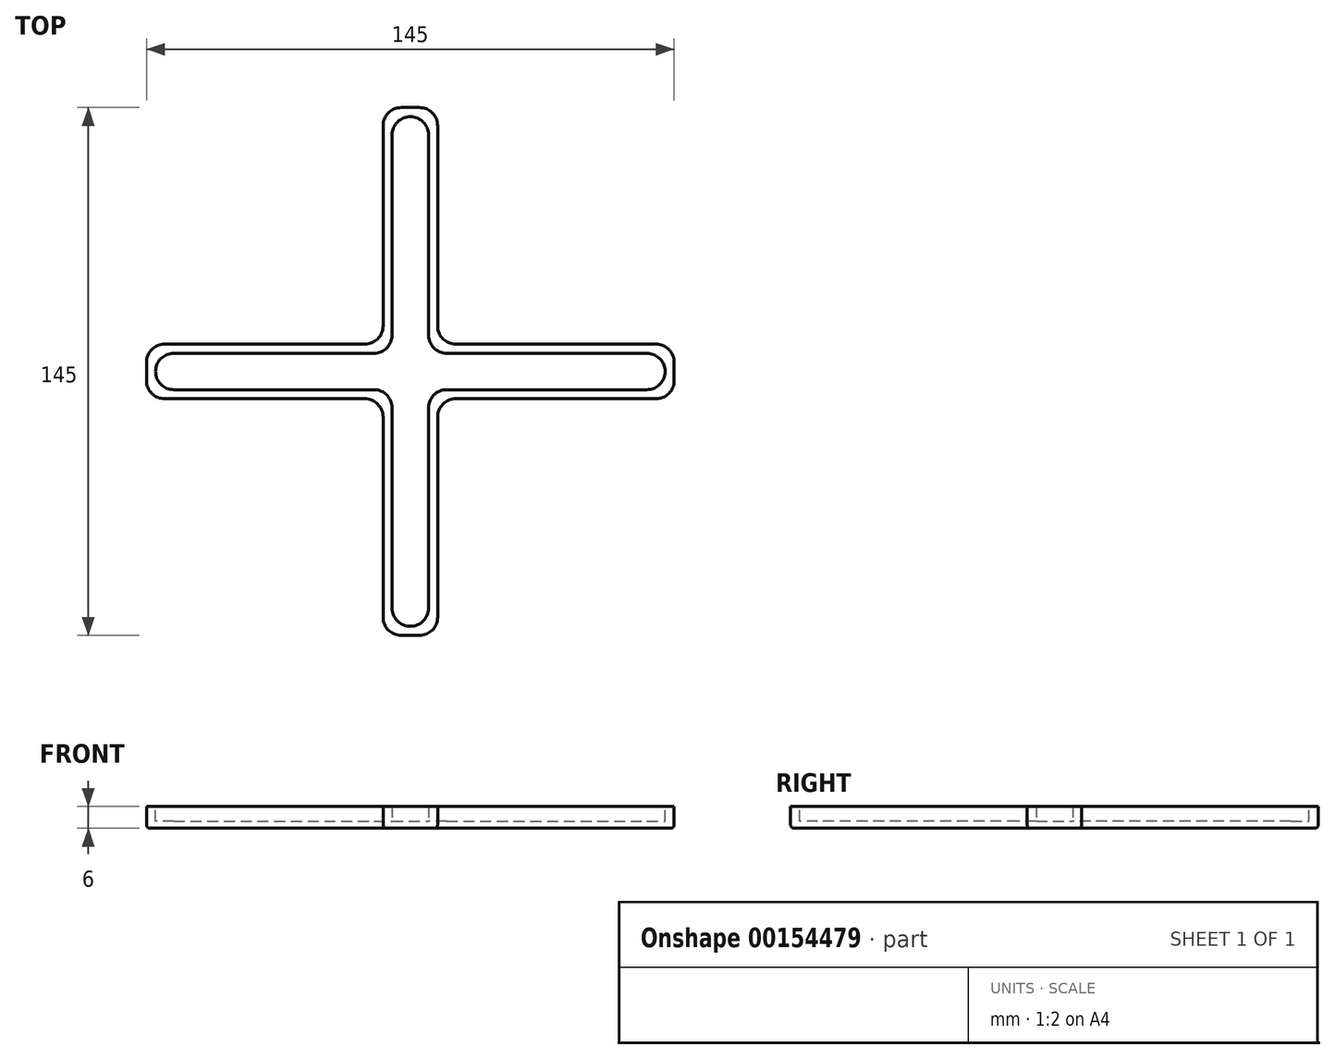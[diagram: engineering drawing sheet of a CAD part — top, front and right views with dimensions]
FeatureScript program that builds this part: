
annotation { "Feature Type Name" : "Feature", "Feature Type Description" : "" }
export const myFeature = defineFeature(function(context is Context, id is Id, definition is map)
    precondition{}
    {
        {
            var Q0;
            Q0=qCreatedBy(makeId("Top.planeOp"),FACE);
            var sketch = newSketch(context, id + "F0", { "sketchPlane" : qUnion([Q0])});
            skLineSegment(sketch, "E0", {"start": v(0, 70) * mm, "end": v(-5, 70) * mm});
            skLineSegment(sketch, "E1", {"start": v(-5, 70) * mm, "end": v(-5, 5) * mm});
            skLineSegment(sketch, "E2", {"start": v(-5, 5) * mm, "end": v(-70, 5) * mm});
            skLineSegment(sketch, "E3", {"start": v(-70, 5) * mm, "end": v(-70, -5) * mm});
            skLineSegment(sketch, "E4", {"start": v(-70, -5) * mm, "end": v(-5, -5) * mm});
            skLineSegment(sketch, "E5", {"start": v(-5, -5) * mm, "end": v(-5, -70) * mm});
            skLineSegment(sketch, "E6", {"start": v(-5, -70) * mm, "end": v(0, -70) * mm});
            skLineSegment(sketch, "E7.MirrorCS", {"start": v(0, 70) * mm, "end": v(5, 70) * mm});
            skLineSegment(sketch, "E8.MirrorCS", {"start": v(5, 70) * mm, "end": v(5, 5) * mm});
            skLineSegment(sketch, "E9.MirrorCS", {"start": v(5, 5) * mm, "end": v(70, 5) * mm});
            skLineSegment(sketch, "E10.MirrorCS", {"start": v(70, 5) * mm, "end": v(70, -5) * mm});
            skLineSegment(sketch, "E11.MirrorCS", {"start": v(70, -5) * mm, "end": v(5, -5) * mm});
            skLineSegment(sketch, "E12.MirrorCS", {"start": v(5, -5) * mm, "end": v(5, -70) * mm});
            skLineSegment(sketch, "E13.MirrorCS", {"start": v(5, -70) * mm, "end": v(0, -70) * mm});
            skLineSegment(sketch, "E14.0", {"start": v(-7.5, 72.5) * mm, "end": v(-7.5, 6.88) * mm});
            skLineSegment(sketch, "E14.1", {"start": v(0, 72.5) * mm, "end": v(-7.5, 72.5) * mm});
            skLineSegment(sketch, "E14.2", {"start": v(0, 72.5) * mm, "end": v(7.5, 72.5) * mm});
            skLineSegment(sketch, "E14.3", {"start": v(-7.5, -72.5) * mm, "end": v(0, -72.5) * mm});
            skLineSegment(sketch, "E14.4", {"start": v(-7.5, -7.5) * mm, "end": v(-7.5, -72.5) * mm});
            skLineSegment(sketch, "E14.5", {"start": v(-72.5, -7.5) * mm, "end": v(-7.5, -7.5) * mm});
            skLineSegment(sketch, "E14.6", {"start": v(-72.5, 6.88) * mm, "end": v(-72.5, -7.5) * mm});
            skLineSegment(sketch, "E14.7", {"start": v(7.5, -72.5) * mm, "end": v(0, -72.5) * mm});
            skLineSegment(sketch, "E14.8", {"start": v(7.5, -7.5) * mm, "end": v(7.5, -72.5) * mm});
            skLineSegment(sketch, "E14.9", {"start": v(72.5, -7.5) * mm, "end": v(7.5, -7.5) * mm});
            skLineSegment(sketch, "E14.10", {"start": v(72.5, 7.5) * mm, "end": v(72.5, -7.5) * mm});
            skLineSegment(sketch, "E14.11", {"start": v(7.5, 7.5) * mm, "end": v(72.5, 7.5) * mm});
            skLineSegment(sketch, "E14.12", {"start": v(7.5, 72.5) * mm, "end": v(7.5, 7.5) * mm});
            skLineSegment(sketch, "E15.0", {"start": v(-7.5, 72.5) * mm, "end": v(-7.5, 7.5) * mm});
            skLineSegment(sketch, "E15.6", {"start": v(-72.5, 7.5) * mm, "end": v(-72.5, -7.5) * mm});
            skLineSegment(sketch, "E15.10", {"start": v(-7.5, 7.5) * mm, "end": v(-72.5, 7.5) * mm});
            skSolve(sketch);
        }
        {
            var Q0;
            Q0=makeQuery(id+"F0.imprint","IMPRINT",FACE,{"disambiguationData":[TD([[makeQuery(id+"F0.imprint","IMPRINT",EDGE,{"derivedFrom":sQuery(id+"F0.wireOp",EDGE,"E0")}),1.0]])]});
            extrude(context, id + "F1", {"entities" : qUnion([Q0]), "depth" : 2 * mm});
        }
        {
            var Q0;
            Q0 = qSketchRegion(id + "F0", true);
            extrude(context, id + "F2", {"entities" : qUnion([Q0]), "operationType" : NewBodyOperationType.ADD, "depth" : 6 * mm});
        }
        {
            var Q0;
            Q0=makeQuery(id+"F2.opExtrude","SWEPT_EDGE",EDGE,{"disambiguationData":[OSD([sQuery(id+"F0.wireOp",EDGE,"E0"),sQuery(id+"F0.wireOp",EDGE,"E1")])]});
            var Q1;
            Q1=makeQuery(id+"F2.opExtrude","SWEPT_EDGE",EDGE,{"disambiguationData":[OSD([sQuery(id+"F0.wireOp",EDGE,"E2"),sQuery(id+"F0.wireOp",EDGE,"E3")])]});
            var Q2;
            Q2=makeQuery(id+"F2.opExtrude","SWEPT_EDGE",EDGE,{"disambiguationData":[OSD([sQuery(id+"F0.wireOp",EDGE,"E7.MirrorCS"),sQuery(id+"F0.wireOp",EDGE,"E8.MirrorCS")])]});
            var Q3;
            Q3=makeQuery(id+"F2.opExtrude","SWEPT_EDGE",EDGE,{"disambiguationData":[OSD([sQuery(id+"F0.wireOp",EDGE,"E9.MirrorCS"),sQuery(id+"F0.wireOp",EDGE,"E10.MirrorCS")])]});
            var Q4;
            Q4=makeQuery(id+"F2.opExtrude","SWEPT_EDGE",EDGE,{"disambiguationData":[OSD([sQuery(id+"F0.wireOp",EDGE,"E10.MirrorCS"),sQuery(id+"F0.wireOp",EDGE,"E11.MirrorCS")])]});
            var Q5;
            Q5=makeQuery(id+"F2.opExtrude","SWEPT_EDGE",EDGE,{"disambiguationData":[OSD([sQuery(id+"F0.wireOp",EDGE,"E12.MirrorCS"),sQuery(id+"F0.wireOp",EDGE,"E13.MirrorCS")])]});
            var Q6;
            Q6=makeQuery(id+"F2.opExtrude","SWEPT_EDGE",EDGE,{"disambiguationData":[OSD([sQuery(id+"F0.wireOp",EDGE,"E3"),sQuery(id+"F0.wireOp",EDGE,"E4")])]});
            var Q7;
            Q7=makeQuery(id+"F2.opExtrude","SWEPT_EDGE",EDGE,{"disambiguationData":[OSD([sQuery(id+"F0.wireOp",EDGE,"E5"),sQuery(id+"F0.wireOp",EDGE,"E6")])]});
            var Q8;
            Q8=makeQuery(id+"F2.opExtrude","SWEPT_EDGE",EDGE,{"disambiguationData":[OSD([sQuery(id+"F0.wireOp",EDGE,"E15.0"),sQuery(id+"F0.wireOp",EDGE,"E14.1")])]});
            var Q9;
            Q9=makeQuery(id+"F2.opExtrude","SWEPT_EDGE",EDGE,{"disambiguationData":[OSD([sQuery(id+"F0.wireOp",EDGE,"E14.2"),sQuery(id+"F0.wireOp",EDGE,"E14.12")])]});
            var Q10;
            Q10=makeQuery(id+"F2.opExtrude","SWEPT_EDGE",EDGE,{"disambiguationData":[OSD([sQuery(id+"F0.wireOp",EDGE,"E14.10"),sQuery(id+"F0.wireOp",EDGE,"E14.11")])]});
            var Q11;
            Q11=makeQuery(id+"F2.opExtrude","SWEPT_EDGE",EDGE,{"disambiguationData":[OSD([sQuery(id+"F0.wireOp",EDGE,"E14.9"),sQuery(id+"F0.wireOp",EDGE,"E14.10")])]});
            var Q12;
            Q12=makeQuery(id+"F2.opExtrude","SWEPT_EDGE",EDGE,{"disambiguationData":[OSD([sQuery(id+"F0.wireOp",EDGE,"E14.7"),sQuery(id+"F0.wireOp",EDGE,"E14.8")])]});
            var Q13;
            Q13=makeQuery(id+"F2.opExtrude","SWEPT_EDGE",EDGE,{"disambiguationData":[OSD([sQuery(id+"F0.wireOp",EDGE,"E15.6"),sQuery(id+"F0.wireOp",EDGE,"E15.10")])]});
            var Q14;
            Q14=makeQuery(id+"F2.opExtrude","SWEPT_EDGE",EDGE,{"disambiguationData":[OSD([sQuery(id+"F0.wireOp",EDGE,"E14.5"),sQuery(id+"F0.wireOp",EDGE,"E15.6")])]});
            var Q15;
            Q15=makeQuery(id+"F2.opExtrude","SWEPT_EDGE",EDGE,{"disambiguationData":[OSD([sQuery(id+"F0.wireOp",EDGE,"E14.3"),sQuery(id+"F0.wireOp",EDGE,"E14.4")])]});
            var Q16;
            Q16=makeQuery(id+"F2.opExtrude","SWEPT_EDGE",EDGE,{"disambiguationData":[OSD([sQuery(id+"F0.wireOp",EDGE,"E14.4"),sQuery(id+"F0.wireOp",EDGE,"E14.5")])]});
            var Q17;
            Q17=makeQuery(id+"F2.opExtrude","SWEPT_EDGE",EDGE,{"disambiguationData":[OSD([sQuery(id+"F0.wireOp",EDGE,"E1"),sQuery(id+"F0.wireOp",EDGE,"E2")])]});
            var Q18;
            Q18=makeQuery(id+"F2.opExtrude","SWEPT_EDGE",EDGE,{"disambiguationData":[OSD([sQuery(id+"F0.wireOp",EDGE,"E8.MirrorCS"),sQuery(id+"F0.wireOp",EDGE,"E9.MirrorCS")])]});
            var Q19;
            Q19=makeQuery(id+"F2.opExtrude","SWEPT_EDGE",EDGE,{"disambiguationData":[OSD([sQuery(id+"F0.wireOp",EDGE,"E11.MirrorCS"),sQuery(id+"F0.wireOp",EDGE,"E12.MirrorCS")])]});
            var Q20;
            Q20=makeQuery(id+"F2.opExtrude","SWEPT_EDGE",EDGE,{"disambiguationData":[OSD([sQuery(id+"F0.wireOp",EDGE,"E15.0"),sQuery(id+"F0.wireOp",EDGE,"E15.10")])]});
            var Q21;
            Q21=makeQuery(id+"F2.opExtrude","SWEPT_EDGE",EDGE,{"disambiguationData":[OSD([sQuery(id+"F0.wireOp",EDGE,"E4"),sQuery(id+"F0.wireOp",EDGE,"E5")])]});
            var Q22;
            Q22=makeQuery(id+"F2.opExtrude","SWEPT_EDGE",EDGE,{"disambiguationData":[OSD([sQuery(id+"F0.wireOp",EDGE,"E14.11"),sQuery(id+"F0.wireOp",EDGE,"E14.12")])]});
            var Q23;
            Q23=makeQuery(id+"F2.opExtrude","SWEPT_EDGE",EDGE,{"disambiguationData":[OSD([sQuery(id+"F0.wireOp",EDGE,"E14.8"),sQuery(id+"F0.wireOp",EDGE,"E14.9")])]});
            fillet(context, id + "F3", {"entities" : qUnion([Q0, Q1, Q2, Q3, Q4, Q5, Q6, Q7, Q8, Q9, Q10, Q11, Q12, Q13, Q14, Q15, Q16, Q17, Q18, Q19, Q20, Q21, Q22, Q23]), "radius" : 5 * mm, "tangentPropagation" : true, "allowEdgeOverflow" : false});
        }
        {
            var Q0;
            Q0=makeQuery(id+"F2.opExtrude","CAP_EDGE",EDGE,{"disambiguationData":[OSD([sQuery(id+"F0.wireOp",EDGE,"E14.12")])],"isStart":true});
            fillet(context, id + "F4", {"entities" : qUnion([Q0]), "radius" : 1 * mm, "tangentPropagation" : true, "allowEdgeOverflow" : false});
        }
    });
